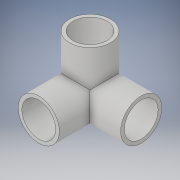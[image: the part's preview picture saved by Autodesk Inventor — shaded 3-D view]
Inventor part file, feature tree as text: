
AUTODESK INVENTOR PART (.ipt)
format: ipt  version: 2018 (Build 220112000, 112)  size: 189,952 bytes
history: native  units: in
note: dims shown in document units (in); Inventor stores cm internally (conversion verified against a paired STEP export)
features: extrude x9, sketch x9, plane x2, revolve x2, projected_geometry x1
ambient origin geometry x8: Origin, YZ Plane, XZ Plane, XY Plane, X Axis, Y Axis, Z Axis, Center Point
bodies: Body1 (feature_tree)
feature tree (23):
  extrude  "Extrusion10"  Depth=2.0in TaperAngle=0.0deg
  sketch  "Sketch24"  dims[d65=90.0deg d66=90.0deg]
  plane  "Work Plane16"
  plane  "Work Plane17"
  sketch  "Sketch25"  dims[d67=1.605in d68=2.0in d69=0.0in]
  extrude  "Extrusion14"  TaperAngle=90.0deg  [1 undecoded]
  extrude  "Extrusion15"  Depth=2.0in TaperAngle=0.0deg
  revolve  "Revolution12"  Angle=90.0deg
  sketch  "Sketch28"  dims[d75=1.0in d76=1.321in]
  sketch  "Sketch29"  dims[d77=1.0in d78=1.321in]
  sketch  "Sketch30"  dims[d79=2.0in d80=0.0in d81=2.0in d82=0.0in]
  extrude  "Extrusion16"  Depth=1.321in
  extrude  "Extrusion17"  Depth=1.321in
  extrude  "Extrusion18"  Depth=1.321in
  extrude  "Extrusion19"  Depth=2.0in TaperAngle=0.0deg
  extrude  "Extrusion20"  Depth=1.25in TaperAngle=0.0deg
  extrude  "Extrusion21"  Depth=1.25in TaperAngle=0.0deg
  revolve  "Revolution13"  [1 undecoded]
  sketch  "Sketch18"  dims[d50=1.605in d51=2.0in d52=0.0in]
  sketch  "Sketch26"  dims[d70=2.0in d71=0.0in d72=90.0deg]
  sketch  "Sketch27"  dims[d73=1.0in d74=1.321in]
  sketch  "Sketch31"  dims[d83=2.0in d84=0.0in d85=1.25in d86=0.0in d87=1.25in d88=0.0in d89=1.25in d90=0.0in d91=0.3779in]
  projected_geometry  "Projected Loop1"
note: 2 required parameter values undecoded (feature->parameter linkage not recoverable at this tier; creation-order binding heuristic only, values carry confidence <= 0.55)